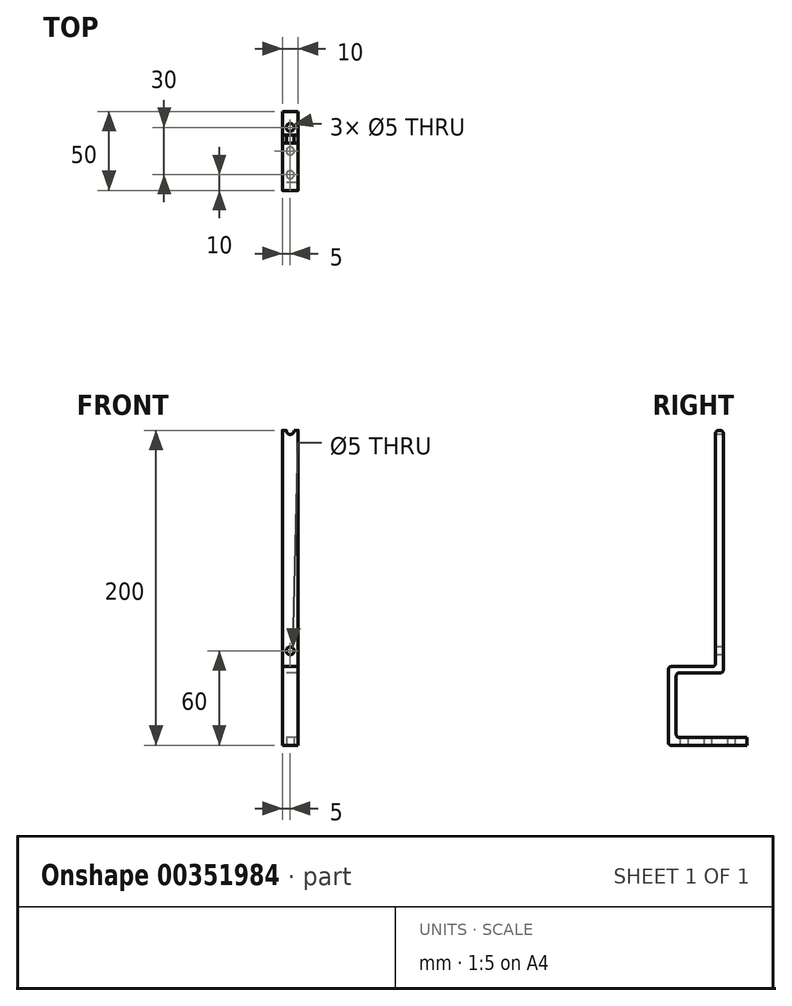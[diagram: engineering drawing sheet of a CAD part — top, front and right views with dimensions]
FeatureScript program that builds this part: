
annotation { "Feature Type Name" : "Feature", "Feature Type Description" : "" }
export const myFeature = defineFeature(function(context is Context, id is Id, definition is map)
    precondition{}
    {
        {
            var Q0;
            Q0=qCreatedBy(makeId("Right.planeOp"),FACE);
            var sketch = newSketch(context, id + "F0", { "sketchPlane" : qUnion([Q0])});
            skLineSegment(sketch, "E0", {"start": v(20, 0) * mm, "end": v(-30, 0) * mm});
            skLineSegment(sketch, "E1", {"start": v(-30, 0) * mm, "end": v(-30, 50) * mm});
            skLineSegment(sketch, "E2", {"start": v(-30, 50) * mm, "end": v(0, 50) * mm});
            skLineSegment(sketch, "E3", {"start": v(0, 50) * mm, "end": v(0, 200) * mm});
            skLineSegment(sketch, "E4", {"start": v(0, 200) * mm, "end": v(5, 200) * mm});
            skLineSegment(sketch, "E5", {"start": v(5, 200) * mm, "end": v(5, 46) * mm});
            skLineSegment(sketch, "E6", {"start": v(5, 46) * mm, "end": v(-25, 46) * mm});
            skLineSegment(sketch, "E7", {"start": v(-25, 46) * mm, "end": v(-25, 5) * mm});
            skLineSegment(sketch, "E8", {"start": v(-25, 5) * mm, "end": v(20, 5) * mm});
            skLineSegment(sketch, "E9", {"start": v(20, 5) * mm, "end": v(20, 0) * mm});
            skSolve(sketch);
        }
        {
            var Q0;
            Q0=makeQuery(id+"F0.imprint","IMPRINT",FACE,{"disambiguationData":[TD([[makeQuery(id+"F0.imprint","IMPRINT",EDGE,{"derivedFrom":sQuery(id+"F0.wireOp",EDGE,"E0")}),-1.0]])]});
            extrude(context, id + "F1", {"entities" : qUnion([Q0]), "depth" : 10 * mm});
        }
        {
            var Q0;
            Q0=makeQuery(id+"F1.opExtrude","SWEPT_FACE",FACE,{"disambiguationData":[OSD([sQuery(id+"F0.wireOp",EDGE,"E3")])]});
            var sketch = newSketch(context, id + "F2", { "sketchPlane" : qUnion([Q0])});
            skCircle(sketch, "E10", {"center": v(5, 200) * mm, "radius": 2.5 * mm});
            skCircle(sketch, "E11", {"center": v(5, 60) * mm, "radius": 2.5 * mm});
            skPoint(sketch, "E11.centerSnap0", {"position": v(5, 50) * mm});
            skSolve(sketch);
        }
        {
            var Q0;
            {var subQ0=sQuery(id+"F2.wireOp",EDGE,"E10");var subQ1=makeQuery(id+"F1.opExtrude","SWEPT_EDGE",EDGE,{"disambiguationData":[OSD([sQuery(id+"F0.wireOp",EDGE,"E3"),sQuery(id+"F0.wireOp",EDGE,"E4")])]});var subQ2=makeQuery(id+"F2.imprint","INTERSECT",VERTEX,{"disambiguationData":[OD(0.0)],"derivedFrom":[subQ1,subQ0]});Q0=makeQuery(id+"F2.imprint","IMPRINT",FACE,{"disambiguationData":[TD([[makeQuery(id+"F2.imprint","IMPRINT",EDGE,{"disambiguationData":[TD([[subQ2,-1.0]])],"derivedFrom":subQ0}),1.0]])]});}
            var Q1;
            Q1=makeQuery(id+"F2.imprint","IMPRINT",FACE,{"disambiguationData":[TD([[makeQuery(id+"F2.imprint","IMPRINT",EDGE,{"derivedFrom":sQuery(id+"F2.wireOp",EDGE,"E11")}),1.0]])]});
            var Q2;
            Q2=makeQuery(id+"F1.opExtrude","SWEPT_FACE",FACE,{"disambiguationData":[OSD([sQuery(id+"F0.wireOp",EDGE,"E5")])]});
            extrude(context, id + "F3", {"entities" : qUnion([Q0, Q1]), "operationType" : NewBodyOperationType.REMOVE, "endBound" : BoundingType.UP_TO_SURFACE, "oppositeDirection" : true, "endBoundEntityFace" : qUnion([Q2]), "depth" : 25 * mm});
        }
        {
            var Q0;
            Q0=makeQuery(id+"F1.opExtrude","SWEPT_FACE",FACE,{"disambiguationData":[OSD([sQuery(id+"F0.wireOp",EDGE,"E0")])]});
            var sketch = newSketch(context, id + "F4", { "sketchPlane" : qUnion([Q0])});
            skCircle(sketch, "E12", {"center": v(5, 20) * mm, "radius": 2.5 * mm});
            skPoint(sketch, "E12.centerSnap0", {"position": v(5, 30) * mm});
            skCircle(sketch, "E13", {"center": v(5, 5) * mm, "radius": 2.5 * mm});
            skCircle(sketch, "E14", {"center": v(5, -10) * mm, "radius": 2.5 * mm});
            skSolve(sketch);
        }
        {
            var Q0;
            Q0=makeQuery(id+"F4.imprint","IMPRINT",FACE,{"disambiguationData":[TD([[makeQuery(id+"F4.imprint","IMPRINT",EDGE,{"derivedFrom":sQuery(id+"F4.wireOp",EDGE,"E12")}),1.0]])]});
            var Q1;
            Q1=makeQuery(id+"F4.imprint","IMPRINT",FACE,{"disambiguationData":[TD([[makeQuery(id+"F4.imprint","IMPRINT",EDGE,{"derivedFrom":sQuery(id+"F4.wireOp",EDGE,"E13")}),1.0]])]});
            var Q2;
            Q2=makeQuery(id+"F4.imprint","IMPRINT",FACE,{"disambiguationData":[TD([[makeQuery(id+"F4.imprint","IMPRINT",EDGE,{"derivedFrom":sQuery(id+"F4.wireOp",EDGE,"E14")}),1.0]])]});
            var Q3;
            Q3=makeQuery(id+"F1.opExtrude","SWEPT_FACE",FACE,{"disambiguationData":[OSD([sQuery(id+"F0.wireOp",EDGE,"E8")])]});
            extrude(context, id + "F5", {"entities" : qUnion([Q0, Q1, Q2]), "operationType" : NewBodyOperationType.REMOVE, "endBound" : BoundingType.UP_TO_SURFACE, "oppositeDirection" : true, "endBoundEntityFace" : qUnion([Q3]), "depth" : 25 * mm});
        }
        {
            var Q0;
            Q0=makeQuery(id+"F1.opExtrude","SWEPT_EDGE",EDGE,{"disambiguationData":[OSD([sQuery(id+"F0.wireOp",EDGE,"E1"),sQuery(id+"F0.wireOp",EDGE,"E2")])]});
            var Q1;
            Q1=makeQuery(id+"F1.opExtrude","SWEPT_EDGE",EDGE,{"disambiguationData":[OSD([sQuery(id+"F0.wireOp",EDGE,"E6"),sQuery(id+"F0.wireOp",EDGE,"E7")])]});
            var Q2;
            Q2=makeQuery(id+"F1.opExtrude","SWEPT_EDGE",EDGE,{"disambiguationData":[OSD([sQuery(id+"F0.wireOp",EDGE,"E0"),sQuery(id+"F0.wireOp",EDGE,"E1")])]});
            var Q3;
            Q3=makeQuery(id+"F1.opExtrude","SWEPT_EDGE",EDGE,{"disambiguationData":[OSD([sQuery(id+"F0.wireOp",EDGE,"E7"),sQuery(id+"F0.wireOp",EDGE,"E8")])]});
            var Q4;
            Q4=makeQuery(id+"F1.opExtrude","SWEPT_EDGE",EDGE,{"disambiguationData":[OSD([sQuery(id+"F0.wireOp",EDGE,"E5"),sQuery(id+"F0.wireOp",EDGE,"E6")])]});
            var Q5;
            Q5=makeQuery(id+"F1.opExtrude","SWEPT_EDGE",EDGE,{"disambiguationData":[OSD([sQuery(id+"F0.wireOp",EDGE,"E2"),sQuery(id+"F0.wireOp",EDGE,"E3")])]});
            var Q6;
            {var subQ0=sQuery(id+"F0.wireOp",EDGE,"E5");var subQ1=sQuery(id+"F0.wireOp",EDGE,"E4");Q6=makeQuery(id+"F3.boolean.opBoolean","SPLIT",EDGE,{"disambiguationData":[TD([makeQuery(id+"F1.opExtrude","CAP_FACE",FACE,{"disambiguationData":[OSD([sQuery(id+"F0.wireOp",EDGE,"E0"),sQuery(id+"F0.wireOp",EDGE,"E1"),sQuery(id+"F0.wireOp",EDGE,"E2"),sQuery(id+"F0.wireOp",EDGE,"E3"),subQ1,subQ0,sQuery(id+"F0.wireOp",EDGE,"E6"),sQuery(id+"F0.wireOp",EDGE,"E7"),sQuery(id+"F0.wireOp",EDGE,"E8"),sQuery(id+"F0.wireOp",EDGE,"E9")])],"isStart":false})])],"derivedFrom":makeQuery(id+"F1.opExtrude","SWEPT_EDGE",EDGE,{"disambiguationData":[OSD([subQ1,subQ0])]})});}
            var Q7;
            {var subQ0=sQuery(id+"F0.wireOp",EDGE,"E4");var subQ1=sQuery(id+"F0.wireOp",EDGE,"E3");Q7=makeQuery(id+"F3.boolean.opBoolean","SPLIT",EDGE,{"disambiguationData":[TD([makeQuery(id+"F1.opExtrude","CAP_FACE",FACE,{"disambiguationData":[OSD([sQuery(id+"F0.wireOp",EDGE,"E0"),sQuery(id+"F0.wireOp",EDGE,"E1"),sQuery(id+"F0.wireOp",EDGE,"E2"),subQ1,subQ0,sQuery(id+"F0.wireOp",EDGE,"E5"),sQuery(id+"F0.wireOp",EDGE,"E6"),sQuery(id+"F0.wireOp",EDGE,"E7"),sQuery(id+"F0.wireOp",EDGE,"E8"),sQuery(id+"F0.wireOp",EDGE,"E9")])],"isStart":false})])],"derivedFrom":makeQuery(id+"F1.opExtrude","SWEPT_EDGE",EDGE,{"disambiguationData":[OSD([subQ1,subQ0])]})});}
            var Q8;
            {var subQ0=sQuery(id+"F0.wireOp",EDGE,"E4");var subQ1=sQuery(id+"F0.wireOp",EDGE,"E3");Q8=makeQuery(id+"F3.boolean.opBoolean","SPLIT",EDGE,{"disambiguationData":[TD([makeQuery(id+"F1.opExtrude","CAP_FACE",FACE,{"disambiguationData":[OSD([sQuery(id+"F0.wireOp",EDGE,"E0"),sQuery(id+"F0.wireOp",EDGE,"E1"),sQuery(id+"F0.wireOp",EDGE,"E2"),subQ1,subQ0,sQuery(id+"F0.wireOp",EDGE,"E5"),sQuery(id+"F0.wireOp",EDGE,"E6"),sQuery(id+"F0.wireOp",EDGE,"E7"),sQuery(id+"F0.wireOp",EDGE,"E8"),sQuery(id+"F0.wireOp",EDGE,"E9")])],"isStart":true})])],"derivedFrom":makeQuery(id+"F1.opExtrude","SWEPT_EDGE",EDGE,{"disambiguationData":[OSD([subQ1,subQ0])]})});}
            var Q9;
            {var subQ0=sQuery(id+"F0.wireOp",EDGE,"E5");var subQ1=sQuery(id+"F0.wireOp",EDGE,"E4");Q9=makeQuery(id+"F3.boolean.opBoolean","SPLIT",EDGE,{"disambiguationData":[TD([makeQuery(id+"F1.opExtrude","CAP_FACE",FACE,{"disambiguationData":[OSD([sQuery(id+"F0.wireOp",EDGE,"E0"),sQuery(id+"F0.wireOp",EDGE,"E1"),sQuery(id+"F0.wireOp",EDGE,"E2"),sQuery(id+"F0.wireOp",EDGE,"E3"),subQ1,subQ0,sQuery(id+"F0.wireOp",EDGE,"E6"),sQuery(id+"F0.wireOp",EDGE,"E7"),sQuery(id+"F0.wireOp",EDGE,"E8"),sQuery(id+"F0.wireOp",EDGE,"E9")])],"isStart":true})])],"derivedFrom":makeQuery(id+"F1.opExtrude","SWEPT_EDGE",EDGE,{"disambiguationData":[OSD([subQ1,subQ0])]})});}
            fillet(context, id + "F6", {"entities" : qUnion([Q0, Q1, Q2, Q3, Q4, Q5, Q6, Q7, Q8, Q9]), "radius" : 2 * mm, "tangentPropagation" : true, "allowEdgeOverflow" : false});
        }
    });
